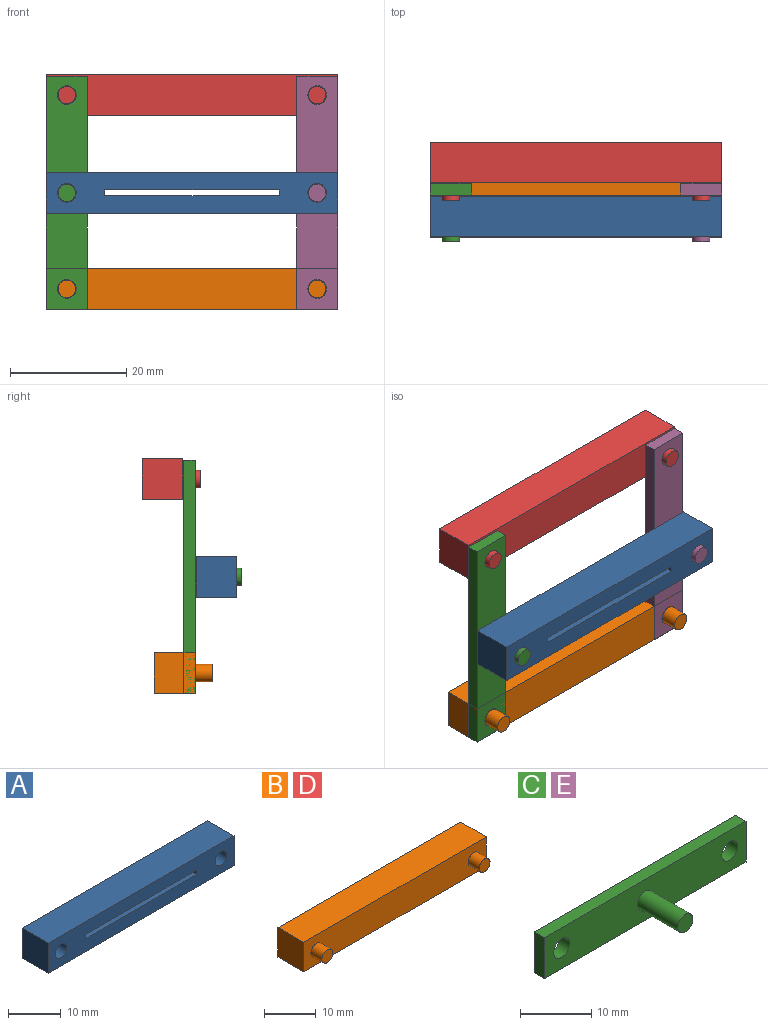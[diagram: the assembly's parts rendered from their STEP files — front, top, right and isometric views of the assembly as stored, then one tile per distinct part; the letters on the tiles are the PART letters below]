
ASSEMBLY  parts=5 mates=6
PART A: 12 faces, bbox 50x7x7 mm
  f0: plane 7x1mm, normal (1,0,0), area 7mm2, adj f1,f7,f10,f11
  f1: plane 30x7mm, normal (0,0,-1), area 210mm2, adj f0,f2,f10,f11
  f2: plane 7x1mm, normal (-1,0,0), area 7mm2, adj f1,f7,f10,f11
  f3: plane 50x7mm, normal (0,0,1), area 350mm2, adj f4,f8,f10,f11
  f4: plane 7x7mm, normal (-1,0,0), area 49mm2, adj f3,f5,f10,f11
  f5: plane 50x7mm, normal (0,0,-1), area 350mm2, adj f4,f8,f10,f11
  f6: cylinder r=1.6mm len=7mm, axis (0,1,0), area 70.4mm2, adj f10,f11
  f7: plane 30x7mm, normal (0,0,1), area 210mm2, adj f0,f2,f10,f11
  f8: plane 7x7mm, normal (1,0,0), area 49mm2, adj f3,f5,f10,f11
  f9: cylinder r=1.6mm len=7mm, axis (0,1,0), area 70.4mm2, adj f10,f11
  f10: plane 50x7mm, normal (0,-1,0), area 303.9mm2, adj f0,f1,f2,f3,f4,f5,f6,f7
  f11: plane 50x7mm, normal (0,1,0), area 303.9mm2, adj f0,f1,f2,f3,f4,f5,f6,f7
PART B: 10 faces, bbox 50x10x7 mm
  f0: plane 50x7mm, normal (0,0,1), area 350mm2, adj f1,f3,f4,f7
  f1: plane 7x7mm, normal (-1,0,0), area 49mm2, adj f0,f2,f4,f7
  f2: plane 50x7mm, normal (0,0,-1), area 350mm2, adj f1,f3,f4,f7
  f3: plane 7x7mm, normal (1,0,0), area 49mm2, adj f0,f2,f4,f7
  f4: plane 50x7mm, normal (0,1,0), area 350mm2, adj f0,f1,f2,f3
  f5: cylinder r=1.5mm len=3mm, axis (0,-1,0), area 28.3mm2, adj f7,f8
  f6: cylinder r=1.5mm len=3mm, axis (0,-1,0), area 28.3mm2, adj f7,f9
  f7: plane 50x7mm, normal (0,-1,0), area 335.9mm2, adj f0,f1,f2,f3,f5,f6
  f8: plane 3x3mm, normal (0,-1,0), area 7.1mm2, adj f5
  f9: plane 3x3mm, normal (0,-1,0), area 7.1mm2, adj f6
PART C: 10 faces, bbox 40x10x7 mm
  f0: plane 40x2mm, normal (0,0,1), area 80mm2, adj f1,f3,f6,f8
  f1: plane 7x2mm, normal (-1,0,0), area 14mm2, adj f0,f2,f6,f8
  f2: plane 40x2mm, normal (0,0,-1), area 80mm2, adj f1,f3,f6,f8
  f3: plane 7x2mm, normal (1,0,0), area 14mm2, adj f0,f2,f6,f8
  f4: cylinder r=1.6mm len=3.2mm, axis (0,1,0), area 20.1mm2, adj f6,f8
  f5: cylinder r=1.6mm len=3.2mm, axis (0,1,0), area 20.1mm2, adj f6,f8
  f6: plane 40x7mm, normal (0,1,0), area 263.9mm2, adj f0,f1,f2,f3,f4,f5
  f7: cylinder r=1.5mm len=8mm, axis (0,-1,0), area 75.4mm2, adj f8,f9
  f8: plane 40x7mm, normal (0,-1,0), area 256.8mm2, adj f0,f1,f2,f3,f4,f5,f7
  f9: plane 3x3mm, normal (0,-1,0), area 7.1mm2, adj f7
PART D: same geometry as B
PART E: same geometry as C
PLACE A rot(axis=(-0.22,-0.98,0.01),0deg) t=(0.92,2.16,-0.03)mm
PLACE B t=(-24.08,9.33,-13.03)mm
PLACE C rot(axis=(0,-1,0),90deg) t=(-24.08,4.33,-20.03)mm
PLACE D t=(-24.08,11.42,20.27)mm
PLACE E rot(axis=(0,-1,0),90deg) t=(18.92,4.33,-20.03)mm
MATE cylindrical E.f5 <-> D.f5  axis (0,-1,0) through (22.42,2.33,16.77)mm
MATE parallel D.f7 <-> B.f7  axis (0,-1,0) through (0.92,4.42,16.77)mm
MATE parallel C.f5 <-> E.f5  axis (0,-1,0) through (-20.58,2.33,16.77)mm
MATE cylindrical B.f5 <-> E.f4  axis (0,-1,0) through (22.42,2.33,-16.53)mm
MATE cylindrical B.f6 <-> C.f4  axis (0,-1,0) through (-20.58,2.33,-16.53)mm
MATE cylindrical C.f5 <-> D.f6  axis (0,-1,0) through (-20.58,2.33,16.77)mm
